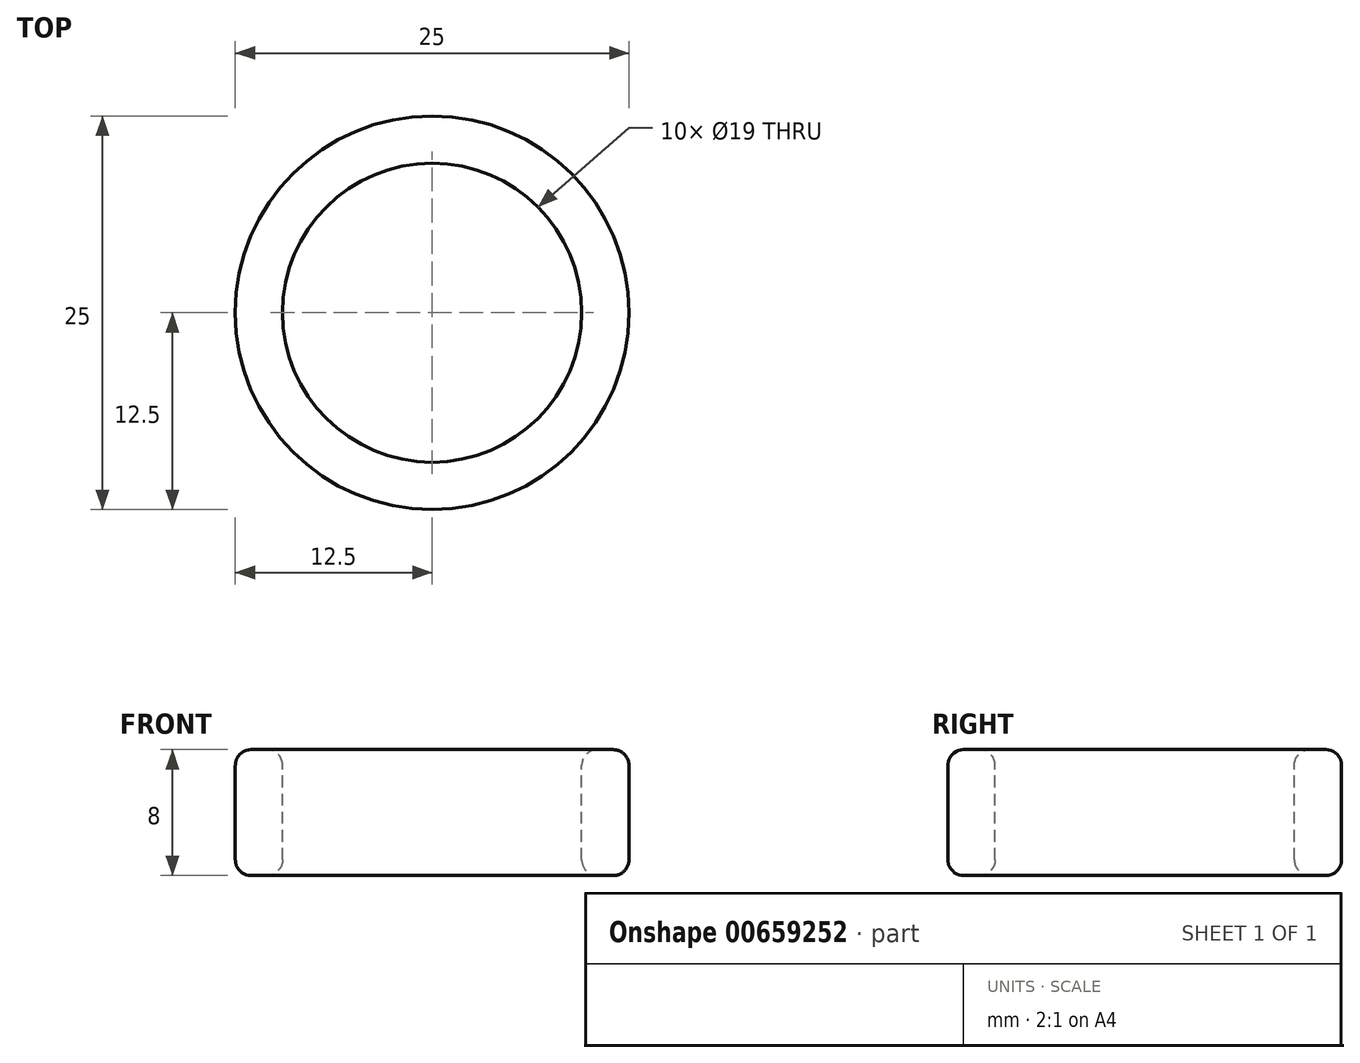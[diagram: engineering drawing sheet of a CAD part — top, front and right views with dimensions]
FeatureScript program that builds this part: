
annotation { "Feature Type Name" : "Feature", "Feature Type Description" : "" }
export const myFeature = defineFeature(function(context is Context, id is Id, definition is map)
    precondition{}
    {
        {
            var Q0;
            Q0=qCreatedBy(makeId("Front.planeOp"),FACE);
            var sketch = newSketch(context, id + "F0", { "sketchPlane" : qUnion([Q0])});
            skLineSegment(sketch, "E0", {"start": v(0, 4.72) * mm, "end": v(0, -3.28) * mm});
            skLineSegment(sketch, "E1.bottom", {"start": v(10.5, 4.72) * mm, "end": v(11.5, 4.72) * mm});
            skLineSegment(sketch, "E1.top", {"start": v(10.5, -3.28) * mm, "end": v(11.5, -3.28) * mm});
            skLineSegment(sketch, "E1.left", {"start": v(12.5, 3.72) * mm, "end": v(12.5, -2.28) * mm});
            skLineSegment(sketch, "E1.right", {"start": v(9.5, 3.72) * mm, "end": v(9.5, -2.28) * mm});
            skPoint(sketch, "E2.visualSharp", {"position": v(12.5, 4.72) * mm});
            skArc(sketch, "E2.filletArc", {"start": v(12.5, 3.72) * mm, "mid": v(12.2, 4.43) * mm, "end": v(11.5, 4.72) * mm});
            skPoint(sketch, "E3.visualSharp", {"position": v(12.5, -3.28) * mm});
            skArc(sketch, "E3.filletArc", {"start": v(11.5, -3.28) * mm, "mid": v(12.2, -2.99) * mm, "end": v(12.5, -2.28) * mm});
            skPoint(sketch, "E4.visualSharp", {"position": v(9.5, 4.72) * mm});
            skArc(sketch, "E4.filletArc", {"start": v(10.5, 4.72) * mm, "mid": v(9.8, 4.43) * mm, "end": v(9.5, 3.72) * mm});
            skPoint(sketch, "E5.visualSharp", {"position": v(9.5, -3.28) * mm});
            skArc(sketch, "E5.filletArc", {"start": v(9.5, -2.28) * mm, "mid": v(9.8, -2.99) * mm, "end": v(10.5, -3.28) * mm});
            skSolve(sketch);
        }
        {
            var Q0;
            Q0=makeQuery(id+"F0.imprint","IMPRINT",FACE,{"disambiguationData":[TD([[makeQuery(id+"F0.imprint","IMPRINT",EDGE,{"derivedFrom":sQuery(id+"F0.wireOp",EDGE,"E1.bottom")}),-1.0]])]});
            var Q1;
            Q1=sQuery(id+"F0.wireOp",EDGE,"E0");
            revolve(context, id + "F1", {"entities" : qUnion([Q0]), "axis" : qUnion([Q1]), "revolveType" : RevolveType.FULL});
        }
    });
